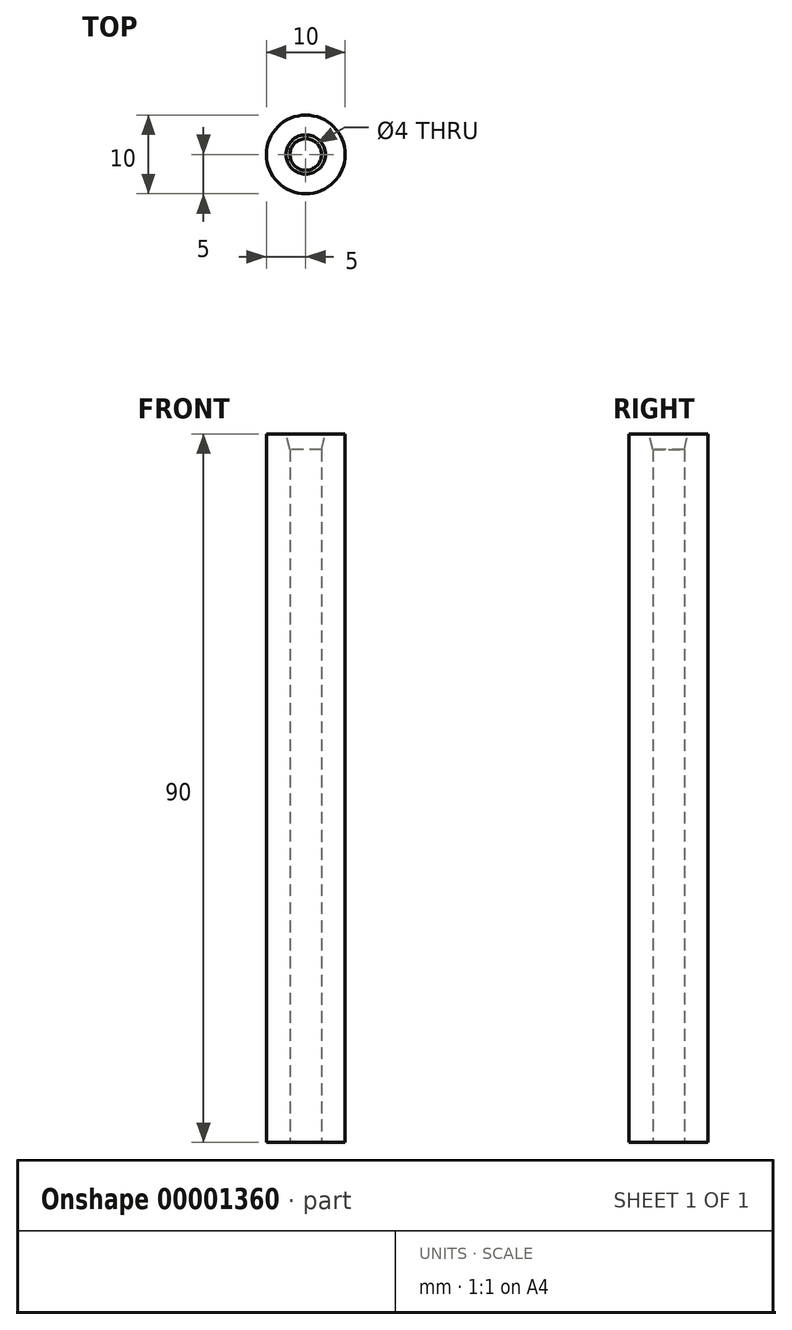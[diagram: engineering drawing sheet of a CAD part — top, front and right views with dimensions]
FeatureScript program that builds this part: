
annotation { "Feature Type Name" : "Feature", "Feature Type Description" : "" }
export const myFeature = defineFeature(function(context is Context, id is Id, definition is map)
    precondition{}
    {
        {
            var Q0;
            Q0=qCreatedBy(makeId("Top.planeOp"),FACE);
            var sketch = newSketch(context, id + "F0", { "sketchPlane" : qUnion([Q0])});
            skCircle(sketch, "E0", {"center": v(0, 0) * mm, "radius": 5 * mm});
            skCircle(sketch, "E1", {"center": v(0, 0) * mm, "radius": 2 * mm});
            skSolve(sketch);
        }
        {
            var Q0;
            Q0 = qSketchRegion(id + "F0", true);
            extrude(context, id + "F1", {"entities" : qUnion([Q0]), "depth" : 90 * mm});
        }
        {
            var Q0;
            Q0=makeQuery(id+"F1.opExtrude","CAP_EDGE",EDGE,{"disambiguationData":[OSD([sQuery(id+"F0.wireOp",EDGE,"E1")])],"isStart":false});
            chamfer(context, id + "F2", {"entities" : qUnion([Q0]), "chamferType" : ChamferType.TWO_OFFSETS, "width1" : .5 * mm, "oppositeDirection" : false, "width2" : 2 * mm, "tangentPropagation" : true});
        }
    });
